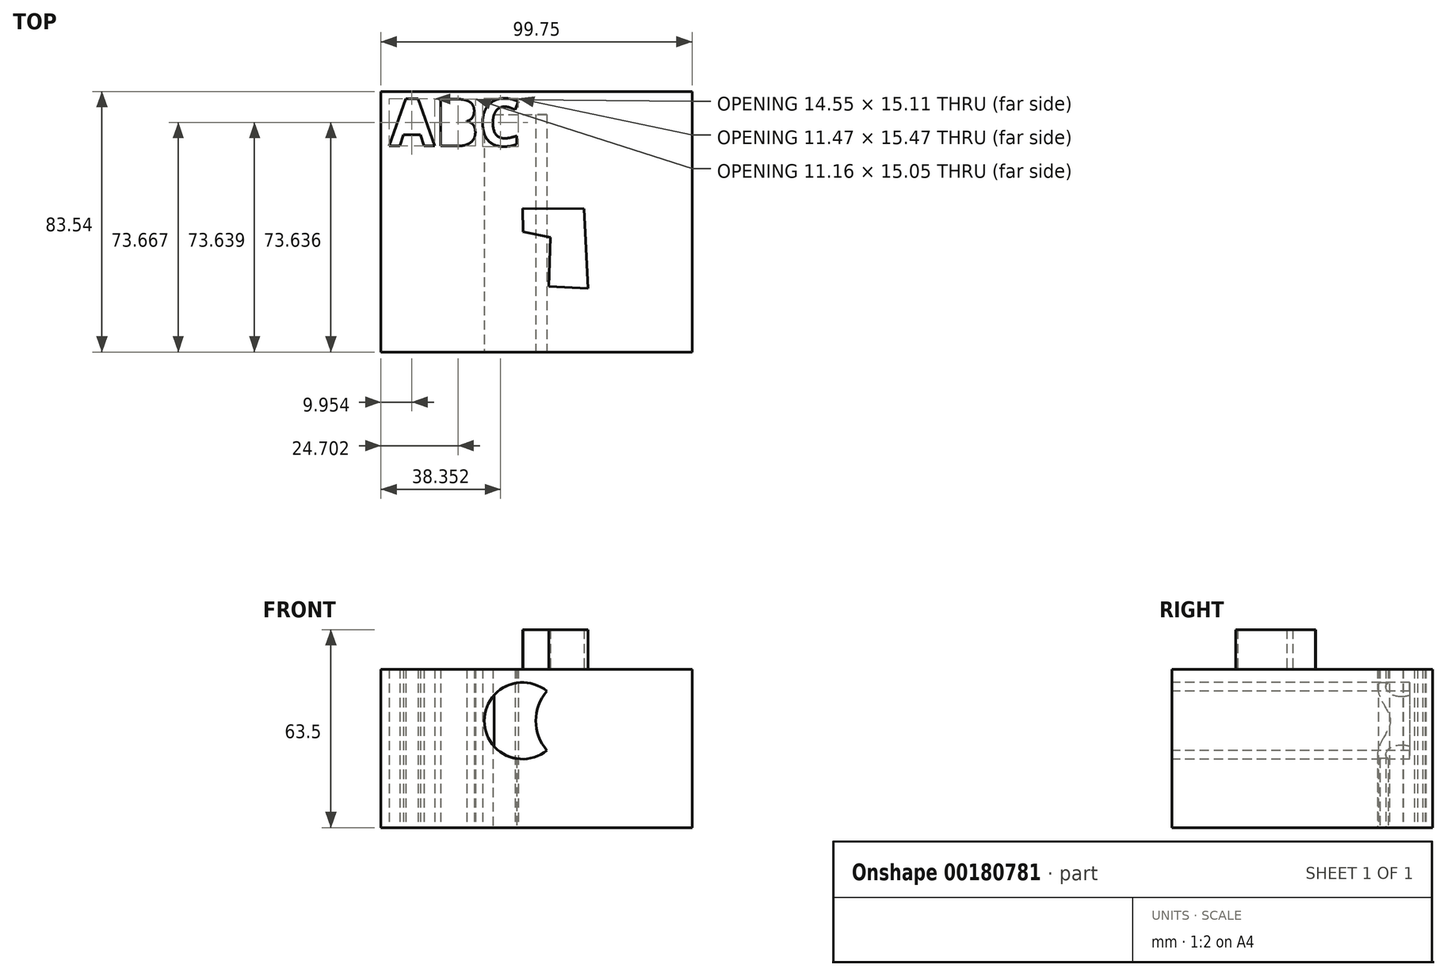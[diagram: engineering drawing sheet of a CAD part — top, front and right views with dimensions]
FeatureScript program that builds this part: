
annotation { "Feature Type Name" : "Feature", "Feature Type Description" : "" }
export const myFeature = defineFeature(function(context is Context, id is Id, definition is map)
    precondition{}
    {
        {
            var Q0;
            Q0=qCreatedBy(makeId("Top.planeOp"),FACE);
            var sketch = newSketch(context, id + "F0", { "sketchPlane" : qUnion([Q0])});
            skLineSegment(sketch, "E0.bottom", {"start": v(-45.45, 37.43) * mm, "end": v(54.3, 37.43) * mm});
            skLineSegment(sketch, "E0.top", {"start": v(-45.45, -46.1) * mm, "end": v(54.3, -46.1) * mm});
            skLineSegment(sketch, "E0.left", {"start": v(-45.45, 37.43) * mm, "end": v(-45.45, -46.1) * mm});
            skLineSegment(sketch, "E0.right", {"start": v(54.3, 37.43) * mm, "end": v(54.3, -46.1) * mm});
            skText(sketch, "E1", { "text": "ABC", "fontName": "OpenSans-Bold.ttf"});
            const initialGuessF0  = {"E1": [-0.04277, 0.02, 1, 0, 0.01518]};
            skSetInitialGuess(sketch, initialGuessF0);
            skSolve(sketch);
        }
        {
            var Q0;
            Q0=makeQuery(id+"F0.imprint","IMPRINT",FACE,{"disambiguationData":[TD([[makeQuery(id+"F0.imprint","IMPRINT",EDGE,{"derivedFrom":sQuery(id+"F0.wireOp",EDGE,"E0.bottom")}),-1.0]])]});
            extrude(context, id + "F1", {"entities" : qUnion([Q0]), "depth" : 50.8 * mm});
        }
        {
            var Q0;
            Q0=makeQuery(id+"F1.opExtrude","SWEPT_FACE",FACE,{"disambiguationData":[OSD([sQuery(id+"F0.wireOp",EDGE,"E0.top")])]});
            var sketch = newSketch(context, id + "F2", { "sketchPlane" : qUnion([Q0])});
            skCircle(sketch, "E2", {"center": v(18.6, 34.25) * mm, "radius": 14.4 * mm});
            skCircle(sketch, "E3", {"center": v(0, 34.25) * mm, "radius": 12.28 * mm});
            skCircle(sketch, "E4", {"center": v(32.06, 29.18) * mm, "radius": 16.46 * mm});
            skCircle(sketch, "E5", {"center": v(32.06, 29.18) * mm, "radius": 5.38 * mm});
            skSolve(sketch);
        }
        {
            var Q0;
            {var subQ0=sQuery(id+"F2.wireOp",EDGE,"E3");var subQ1=sQuery(id+"F2.wireOp",EDGE,"E2");var subQ2=makeQuery(id+"F2.imprint","INTERSECT",VERTEX,{"disambiguationData":[OD(0.0)],"derivedFrom":[subQ1,subQ0]});Q0=makeQuery(id+"F2.imprint","IMPRINT",FACE,{"disambiguationData":[TD([[makeQuery(id+"F2.imprint","IMPRINT",EDGE,{"disambiguationData":[TD([[subQ2,-1.0]])],"derivedFrom":subQ1}),-1.0]])]});}
            extrude(context, id + "F3", {"entities" : qUnion([Q0]), "operationType" : NewBodyOperationType.REMOVE, "oppositeDirection" : true, "depth" : 76.2 * mm});
        }
        {
            var Q0;
            Q0=makeQuery(id+"F1.opExtrude","CAP_FACE",FACE,{"disambiguationData":[OSD([sQuery(id+"F0.wireOp",EDGE,"E0.bottom"),sQuery(id+"F0.wireOp",EDGE,"E0.top"),sQuery(id+"F0.wireOp",EDGE,"E0.left"),sQuery(id+"F0.wireOp",EDGE,"E0.right"),sQuery(id+"F0.wireOp",EDGE,"E1.sketch_text.stroke-0"),sQuery(id+"F0.wireOp",EDGE,"E1.sketch_text.stroke-1"),sQuery(id+"F0.wireOp",EDGE,"E1.sketch_text.stroke-2"),sQuery(id+"F0.wireOp",EDGE,"E1.sketch_text.stroke-3"),sQuery(id+"F0.wireOp",EDGE,"E1.sketch_text.stroke-4"),sQuery(id+"F0.wireOp",EDGE,"E1.sketch_text.stroke-5"),sQuery(id+"F0.wireOp",EDGE,"E1.sketch_text.stroke-6"),sQuery(id+"F0.wireOp",EDGE,"E1.sketch_text.stroke-7"),sQuery(id+"F0.wireOp",EDGE,"E1.sketch_text.stroke-12"),sQuery(id+"F0.wireOp",EDGE,"E1.sketch_text.stroke-13"),sQuery(id+"F0.wireOp",EDGE,"E1.sketch_text.stroke-14"),sQuery(id+"F0.wireOp",EDGE,"E1.sketch_text.stroke-15"),sQuery(id+"F0.wireOp",EDGE,"E1.sketch_text.stroke-16"),sQuery(id+"F0.wireOp",EDGE,"E1.sketch_text.stroke-17"),sQuery(id+"F0.wireOp",EDGE,"E1.sketch_text.stroke-18"),sQuery(id+"F0.wireOp",EDGE,"E1.sketch_text.stroke-19"),sQuery(id+"F0.wireOp",EDGE,"E1.sketch_text.stroke-20"),sQuery(id+"F0.wireOp",EDGE,"E1.sketch_text.stroke-21"),sQuery(id+"F0.wireOp",EDGE,"E1.sketch_text.stroke-22"),sQuery(id+"F0.wireOp",EDGE,"E1.sketch_text.stroke-23"),sQuery(id+"F0.wireOp",EDGE,"E1.sketch_text.stroke-37"),sQuery(id+"F0.wireOp",EDGE,"E1.sketch_text.stroke-38"),sQuery(id+"F0.wireOp",EDGE,"E1.sketch_text.stroke-39"),sQuery(id+"F0.wireOp",EDGE,"E1.sketch_text.stroke-40"),sQuery(id+"F0.wireOp",EDGE,"E1.sketch_text.stroke-41"),sQuery(id+"F0.wireOp",EDGE,"E1.sketch_text.stroke-42"),sQuery(id+"F0.wireOp",EDGE,"E1.sketch_text.stroke-43"),sQuery(id+"F0.wireOp",EDGE,"E1.sketch_text.stroke-44"),sQuery(id+"F0.wireOp",EDGE,"E1.sketch_text.stroke-45"),sQuery(id+"F0.wireOp",EDGE,"E1.sketch_text.stroke-46"),sQuery(id+"F0.wireOp",EDGE,"E1.sketch_text.stroke-47"),sQuery(id+"F0.wireOp",EDGE,"E1.sketch_text.stroke-48"),sQuery(id+"F0.wireOp",EDGE,"E1.sketch_text.stroke-49"),sQuery(id+"F0.wireOp",EDGE,"E1.sketch_text.stroke-50"),sQuery(id+"F0.wireOp",EDGE,"E1.sketch_text.stroke-51")])],"isStart":false});
            var sketch = newSketch(context, id + "F4", { "sketchPlane" : qUnion([Q0])});
            skLineSegment(sketch, "E6", {"start": v(0, 0) * mm, "end": v(19.72, -0.13) * mm});
            skLineSegment(sketch, "E7", {"start": v(19.72, -0.13) * mm, "end": v(21.01, -25.67) * mm});
            skLineSegment(sketch, "E8", {"start": v(8.83, -9.34) * mm, "end": v(8.38, -25.02) * mm});
            skPoint(sketch, "E9.orphan", {"position": v(-2.71, -24.36) * mm});
            skPoint(sketch, "E10.orphan", {"position": v(0, -25.21) * mm});
            skPoint(sketch, "E11.orphan", {"position": v(9.15, -25.02) * mm});
            skLineSegment(sketch, "E12", {"start": v(8.38, -25.02) * mm, "end": v(21.01, -25.67) * mm});
            skLineSegment(sketch, "E13", {"start": v(0, 0) * mm, "end": v(0.1, -7.47) * mm});
            skLineSegment(sketch, "E14", {"start": v(0.1, -7.47) * mm, "end": v(8.83, -9.34) * mm});
            skSolve(sketch);
        }
        {
            var Q0;
            Q0=makeQuery(id+"F4.imprint","IMPRINT",FACE,{"disambiguationData":[TD([[makeQuery(id+"F4.imprint","IMPRINT",EDGE,{"derivedFrom":sQuery(id+"F4.wireOp",EDGE,"E6")}),-1.0]])]});
            extrude(context, id + "F5", {"entities" : qUnion([Q0]), "operationType" : NewBodyOperationType.ADD, "depth" : 12.7 * mm});
        }
    });
